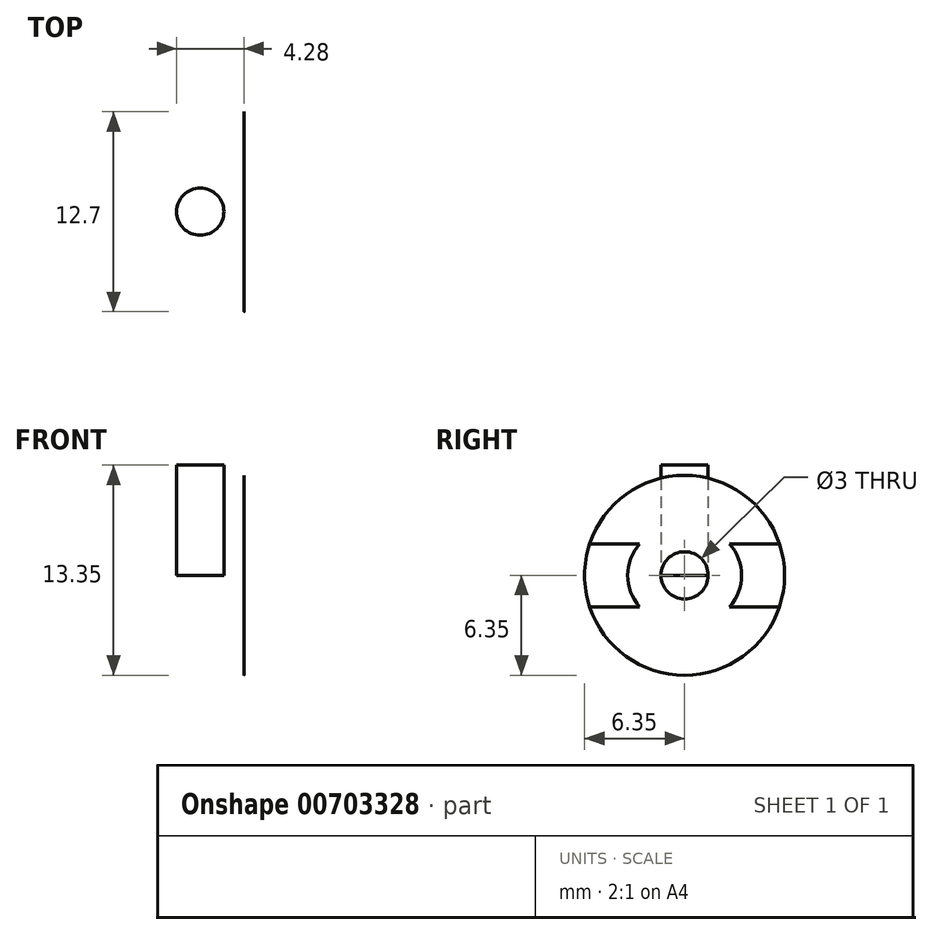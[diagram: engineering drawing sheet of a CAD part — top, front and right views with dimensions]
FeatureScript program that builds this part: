
annotation { "Feature Type Name" : "Feature", "Feature Type Description" : "" }
export const myFeature = defineFeature(function(context is Context, id is Id, definition is map)
    precondition{}
    {
        {
            var Q0;
            Q0=qCreatedBy(makeId("Right.planeOp"),FACE);
            var sketch = newSketch(context, id + "F0", { "sketchPlane" : qUnion([Q0])});
            skCircle(sketch, "E0", {"center": v(0, 0) * mm, "radius": 6.35 * mm});
            skCircle(sketch, "E1", {"center": v(0, 0) * mm, "radius": 1.5 * mm});
            skLineSegment(sketch, "E2", {"start": v(-6.03, 2) * mm, "end": v(-2.85, 2) * mm});
            skLineSegment(sketch, "E3", {"start": v(-6.03, -2) * mm, "end": v(-2.85, -2) * mm});
            skLineSegment(sketch, "E4", {"start": v(6.03, 2) * mm, "end": v(2.85, 2) * mm});
            skLineSegment(sketch, "E5", {"start": v(6.03, -2) * mm, "end": v(2.85, -2) * mm});
            skArc(sketch, "E6", {"start": v(-2.85, 2) * mm, "mid": v(-3.62, 0) * mm, "end": v(-2.85, -2) * mm});
            skArc(sketch, "E7", {"start": v(2.85, -2) * mm, "mid": v(3.62, 0) * mm, "end": v(2.85, 2) * mm});
            skSolve(sketch);
        }
        {
            var Q0;
            Q0=makeQuery(id+"F0.imprint","IMPRINT",FACE,{"disambiguationData":[TD([[makeQuery(id+"F0.imprint","IMPRINT",EDGE,{"derivedFrom":sQuery(id+"F0.wireOp",EDGE,"E1")}),-1.0]])]});
            var Q1;
            {var subQ0=sQuery(id+"F0.wireOp",EDGE,"E2");Q1=makeQuery(id+"F0.imprint","IMPRINT",FACE,{"disambiguationData":[TD([[makeQuery(id+"F0.imprint","IMPRINT",EDGE,{"derivedFrom":subQ0}),-1.0]])]});}
            var Q2;
            {var subQ0=sQuery(id+"F0.wireOp",EDGE,"E4");Q2=makeQuery(id+"F0.imprint","IMPRINT",FACE,{"disambiguationData":[TD([[makeQuery(id+"F0.imprint","IMPRINT",EDGE,{"derivedFrom":subQ0}),1.0]])]});}
            extrude(context, id + "F1", {"entities" : qUnion([Q0, Q1, Q2]), "depth" : -7 / 812.8 * mm, "offsetDistance" : 25 * mm});
        }
        {
            var Q0;
            {var subQ0=sQuery(id+"F0.wireOp",EDGE,"E2");Q0=makeQuery(id+"F0.imprint","IMPRINT",FACE,{"disambiguationData":[TD([[makeQuery(id+"F0.imprint","IMPRINT",EDGE,{"derivedFrom":subQ0}),-1.0]])]});}
            var Q1;
            {var subQ0=sQuery(id+"F0.wireOp",EDGE,"E4");Q1=makeQuery(id+"F0.imprint","IMPRINT",FACE,{"disambiguationData":[TD([[makeQuery(id+"F0.imprint","IMPRINT",EDGE,{"derivedFrom":subQ0}),1.0]])]});}
            extrude(context, id + "F2", {"entities" : qUnion([Q0, Q1]), "operationType" : NewBodyOperationType.ADD, "depth" : 5 / 1625.6 * mm, "offsetDistance" : 25 * mm});
        }
        {
            var Q0;
            Q0=qCreatedBy(makeId("Top.planeOp"),FACE);
            var sketch = newSketch(context, id + "F3", { "sketchPlane" : qUnion([Q0])});
            skCircle(sketch, "E8", {"center": v(-2.78, 0) * mm, "radius": 1.5 * mm});
            skLineSegment(sketch, "E9", {"start": v(0, 0) * mm, "end": v(-2.78, 0) * mm});
            skSolve(sketch);
        }
        {
            var Q0;
            Q0=makeQuery(id+"F3.imprint","IMPRINT",FACE,{"disambiguationData":[TD([[makeQuery(id+"F3.imprint","IMPRINT",EDGE,{"derivedFrom":sQuery(id+"F3.wireOp",EDGE,"E8")}),1.0]])]});
            extrude(context, id + "F4", {"entities" : qUnion([Q0]), "operationType" : NewBodyOperationType.ADD, "depth" : 7 * mm, "offsetDistance" : 25 * mm});
        }
    });
